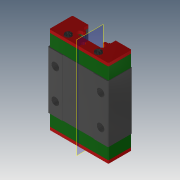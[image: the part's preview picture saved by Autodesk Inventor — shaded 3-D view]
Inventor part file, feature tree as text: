
AUTODESK INVENTOR PART (.ipt)
format: ipt  version: 2022 (Build 260153000, 153)  size: 479,744 bytes
history: native  units: mm
features: plane x1
ambient origin geometry x8: Origin, YZ Plane, XZ Plane, XY Plane, X Axis, Y Axis, Z Axis, Center Point
bodies: Volumenkörper2 (feature_tree), Volumenkörper1 (feature_tree)
feature tree (1):
  plane  "Arbeitsebene1"
